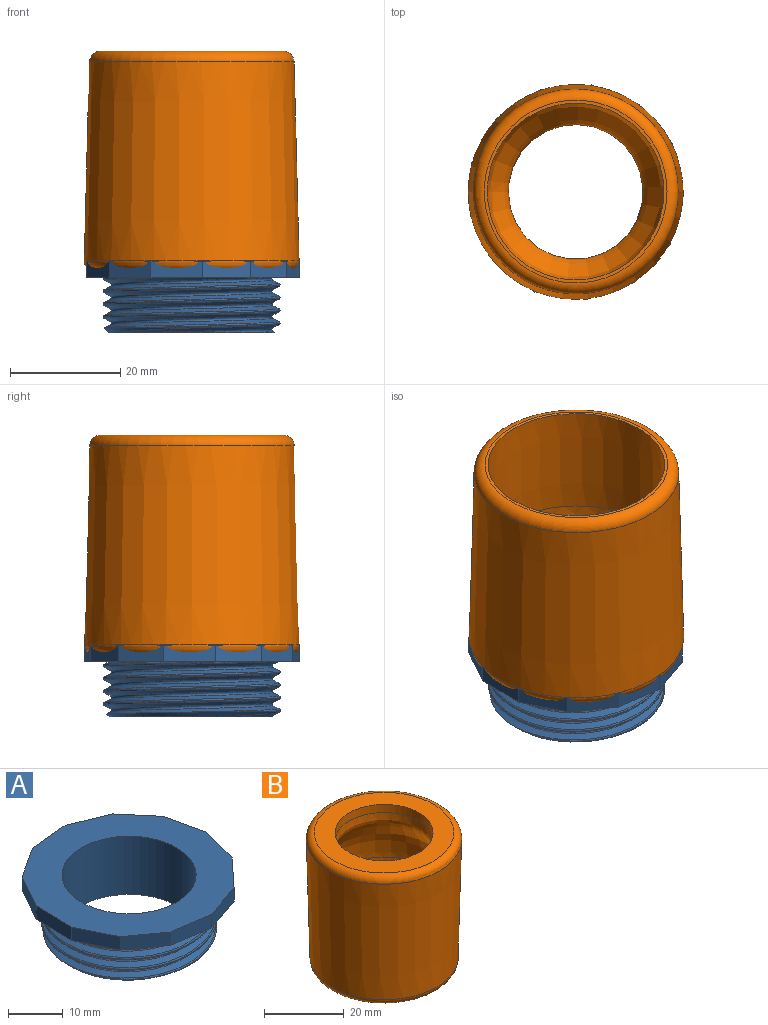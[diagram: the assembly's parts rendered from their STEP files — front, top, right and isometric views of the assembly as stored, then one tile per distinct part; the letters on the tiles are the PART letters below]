
ASSEMBLY  parts=2 mates=1
PART A: 25 faces, bbox 39.3x39.5x14.5 mm
  f0: plane 39.45x39.28mm, normal (0,0,-1), area 423.1mm2, adj f1,f2,f3,f4,f5,f6,f7,f8
  f1: plane 8.19x4.55mm, normal (-0.87,0.49,0), area 28.1mm2, adj f0,f2,f13,f14
  f2: plane 9.36x3mm, normal (-1,0.02,0), area 28.1mm2, adj f0,f1,f3,f14
  f3: plane 8.39x4.16mm, normal (-0.9,-0.44,0), area 28.1mm2, adj f0,f2,f4,f14
  f4: plane 7.58x5.5mm, normal (-0.59,-0.81,0), area 28.1mm2, adj f0,f3,f5,f14
  f5: plane 9.27x3mm, normal (-0.14,-0.99,0), area 28.1mm2, adj f0,f4,f6,f14
  f6: plane 8.83x3.11mm, normal (0.33,-0.94,0), area 28.1mm2, adj f0,f5,f7,f14
  f7: plane 6.86x6.37mm, normal (0.73,-0.68,0), area 28.1mm2, adj f0,f6,f8,f14
  f8: plane 9.04x3mm, normal (0.97,-0.26,0), area 28.1mm2, adj f0,f7,f9,f14
  f9: plane 9.14x3mm, normal (0.98,0.22,0), area 28.1mm2, adj f0,f8,f10,f14
  f10: plane 7.16x6.04mm, normal (0.76,0.65,0), area 28.1mm2, adj f0,f9,f11,f14
  f11: plane 8.68x3.53mm, normal (0.38,0.93,0), area 28.1mm2, adj f0,f10,f12,f14
  f12: plane 9.32x3mm, normal (-0.1,1,0), area 28.1mm2, adj f0,f11,f13,f14
  f13: plane 7.83x5.14mm, normal (-0.55,0.84,0), area 28.1mm2, adj f0,f1,f12,f14
  f14: plane 38.84x38.67mm, normal (0,0,1), area 685.3mm2, adj f1,f2,f3,f4,f5,f6,f7,f8
  f15: cylinder r=16mm len=32mm, axis (0,0,1), area -1.1mm2, adj f0,f19,f20,f22,f23
  f16: bspline ~33.93x29.38mm, area 273.1mm2, adj f0,f17,f18,f21
  f17: bspline ~36.56x31.66mm, area 515.9mm2, adj f0,f16,f19,f21,f22,f23
  f18: bspline ~36.56x31.66mm, area 515.7mm2, adj f0,f16,f20,f21,f22
  f19: plane 0.31x0.21mm, normal (0.35,0.94,0), area 0mm2, adj f0,f15,f17,f23
  f20: bspline ~36.95x32mm, area 135.4mm2, adj f0,f15,f18,f22
  f21: plane 30.22x29.74mm, normal (0,0,-1), area 223.8mm2, adj f16,f17,f18,f22,f24
  f22: cone r=16mm half-angle=45deg, axis (0,0,1), area 50.6mm2, adj f15,f17,f18,f20,f21,f23
  f23: bspline ~31.96x31.95mm, area 132.8mm2, adj f15,f17,f19,f22
  f24: cylinder r=12.25mm len=24.5mm, axis (0,0,1), area 1000.6mm2, adj f14,f21
PART B: 8 faces, bbox 42.1x42.1x40 mm
  f0: cone r=16.52mm half-angle=1.4deg, axis (0,0,1), area 2128.8mm2, adj f1,f5
  f1: revolved ~33.06x33.06mm, area 1625.4mm2, adj f0,f2
  f2: cylinder r=12.25mm len=24.5mm, axis (0,0,-1), area 192.4mm2, adj f1,f3
  f3: plane 34.9x34.9mm, normal (0,0,1), area 485.1mm2, adj f2,f6
  f4: cone r=18.5mm half-angle=1.4deg, axis (0,0,1), area 4298.8mm2, adj f6,f7
  f5: plane 33.1x33.1mm, normal (0,0,-1), area 56.2mm2, adj f0,f7
  f6: torus R=17.45mm, axis (0,0,1), area 375.7mm2, adj f3,f4
  f7: torus R=16.55mm, axis (0,0,1), area 346mm2, adj f4,f5
PLACE A t=(-37.09,14.23,59.02)mm
PLACE B rot(axis=(1,0,0),180deg) t=(-37.09,14.23,98.02)mm
MATE fastened B.f0 <-> A.f24  axis (0,0,-1) through (-37.09,14.23,58.02)mm
